# Revit family: Lighting_Device-Relay-Hubbell_Wiring-AAR
name_source: partatom
category: Lighting Devices
revit_build: Autodesk Revit MEP 2012 (Build: 20110916_2132(x64)
units: mm (PartAtom-declared; Revit-internal decimal feet)

## types (2) — shared parameters
Automatic ON = Yes
Certifications = Plenum Rated, cULus
Connector Description 1 = Direct Current Power Supply
Connector Description 2 = Controls
DC Voltage = 24 V
Frequency = 60 Hz
Humidity = 0% to 90% non condensing 
relative humidity
Load Classification = Transformer
Manual ON = Yes
Manufacturer = Hubbell Wiring Device-Kellems
Number of Poles = 1
Power Factor = 1
Product Documentation Link = http://ecatalog.hubbell-wiring.com
Product Material = Plastic - Hubbell - Black
Product Page URL = http://www.hubbell-wiring.com
URL = http://www.hubbell-wiring.com
zero-valued in all types: Default Elevation

## per-type parameters (varying)
| type | Apparent Load | Description | Operating Temperature | UPC Number |
| AAR | 0.800 VA | For use with CU series control units and Hubbell ATD, ATU and ATP series 
ceiling and wall mount sensors
ceiling/wall mount sensors | 32°F to 104°F (0°C to 40°C) | 783585392653 |
| AAR20P | 0.025 VA | Heavy duty latching relay; for use with CU300HD in Plug load applications
ceiling/wall mount sensors | -40°F to 149°F (-40°C to 65°C) |  |

note: column(s) folded — value = type name in every type: Model, Type Selector

## geometry (parser evidence)
native form markers: Sweep x6
no freeform markers — native parametric forms only
